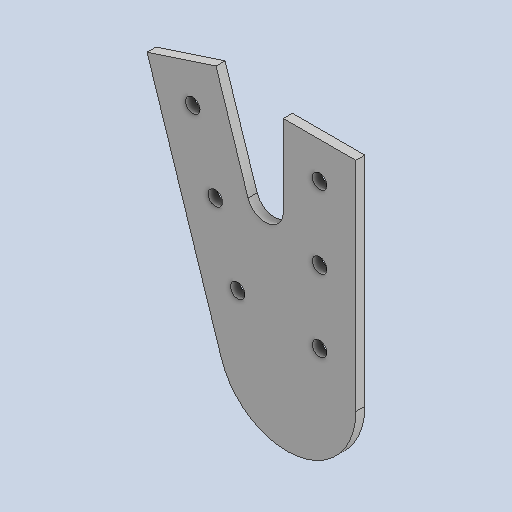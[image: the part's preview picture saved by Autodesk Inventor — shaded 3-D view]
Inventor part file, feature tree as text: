
AUTODESK INVENTOR PART (.ipt)
format: ipt  version: 2024 (Build 280153000, 153)  size: 169,984 bytes
history: native  units: in
note: dims shown in document units (in); Inventor stores cm internally (conversion verified against a paired STEP export)
features: extrude x2, fillet x1, projected_geometry x1
ambient origin geometry x8: Origin, YZ Plane, XZ Plane, XY Plane, X Axis, Y Axis, Z Axis, Center Point
bodies: Solid1 (feature_tree)
feature tree (4):
  extrude  "Extrusion1"  Depth=1.0in
  fillet  "Fillet1"  Radius=3.0in
  extrude  "Extrusion2"  Depth=1.0in
  projected_geometry  "Projected Loop1"
